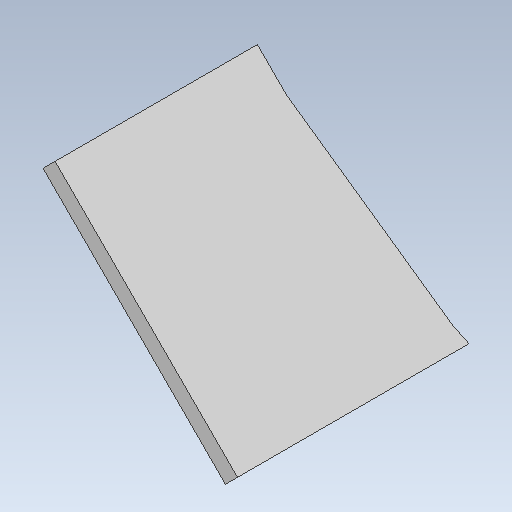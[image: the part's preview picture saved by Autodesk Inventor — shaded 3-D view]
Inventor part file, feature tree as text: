
AUTODESK INVENTOR PART (.ipt)
format: ipt  version: 2020 (Build 240168000, 168)  size: 88,576 bytes
history: native  units: mm
features: other x4, sketch x3
ambient origin geometry x8: Origin, YZ Plane, XZ Plane, XY Plane, X Axis, Y Axis, Z Axis, Center Point
bodies: Body1 (feature_tree)
feature tree (7):
  other  "diagonal.ipt"
  other  "Sólido1::diagonal.ipt"
  other  "OperaçãoIdentificador1"
  sketch  "Esboço1"  dims[d0=10.0mm]
  sketch  "Esboço3"
  sketch  "Esboço6"
  other  "Sólido1"
